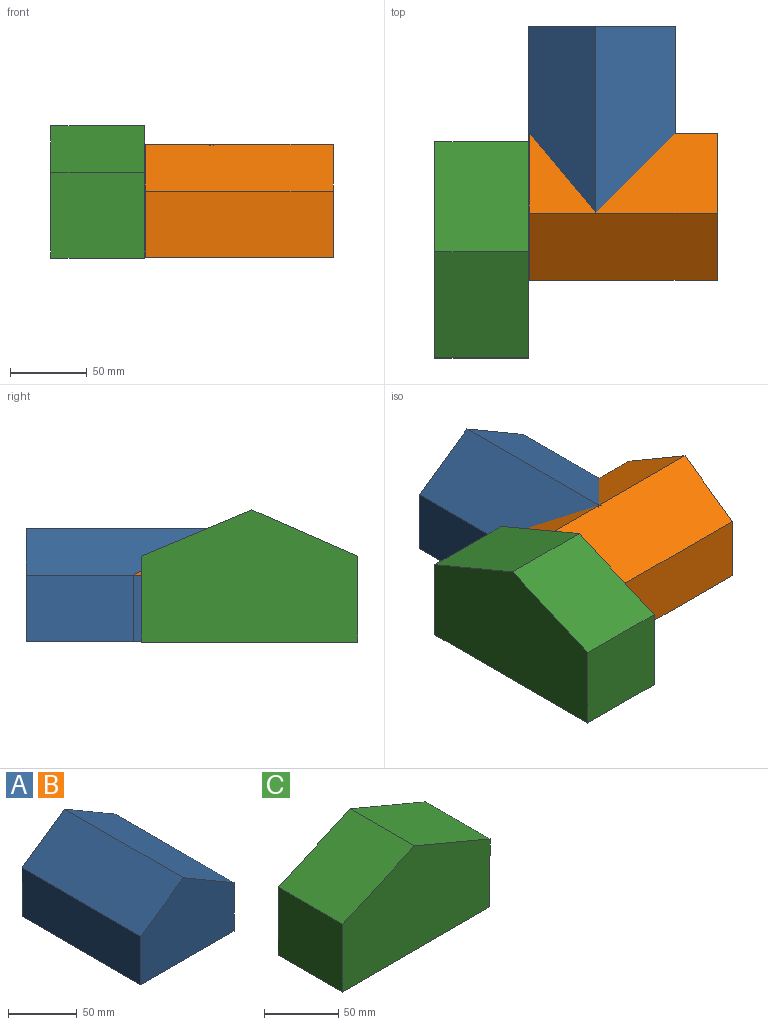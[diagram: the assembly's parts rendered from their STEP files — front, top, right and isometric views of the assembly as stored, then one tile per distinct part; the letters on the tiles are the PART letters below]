
ASSEMBLY  parts=3 mates=3
PART A: 7 faces, bbox 95.5x121.9x73.4 mm
  f0: plane 121.92x43.51mm, normal (-0.57,0,0.82), area 6476.6mm2, adj f1,f4,f5,f6
  f1: plane 121.92x42.97mm, normal (-1,0,0), area 5238.6mm2, adj f0,f2,f5,f6
  f2: plane 121.92x95.52mm, normal (0,0,-1), area 11645.4mm2, adj f1,f3,f5,f6
  f3: plane 121.92x42.97mm, normal (1,0,0), area 5238.6mm2, adj f2,f4,f5,f6
  f4: plane 121.92x52mm, normal (0.51,0,0.86), area 7348.2mm2, adj f0,f3,f5,f6
  f5: plane 95.52x73.44mm, normal (0,-1,0), area 5559.3mm2, adj f0,f1,f2,f3,f4
  f6: plane 95.52x73.44mm, normal (0,1,0), area 5559.3mm2, adj f0,f1,f2,f3,f4
PART B: same geometry as A
PART C: 7 faces, bbox 140.3x61x85.8 mm
  f0: plane 68.82x60.96mm, normal (-0.4,0,0.92), area 4577.2mm2, adj f1,f4,f5,f6
  f1: plane 60.96x55.82mm, normal (-1,0,0), area 3402.9mm2, adj f0,f2,f5,f6
  f2: plane 140.33x60.96mm, normal (0,0,-1), area 8554.5mm2, adj f1,f3,f5,f6
  f3: plane 60.96x55.82mm, normal (1,0,0), area 3402.9mm2, adj f2,f4,f5,f6
  f4: plane 71.51x60.96mm, normal (0.39,0,0.92), area 4727.6mm2, adj f0,f3,f5,f6
  f5: plane 140.33x85.84mm, normal (0,-1,0), area 9939.8mm2, adj f0,f1,f2,f3,f4
  f6: plane 140.33x85.84mm, normal (0,1,0), area 9939.8mm2, adj f0,f1,f2,f3,f4
PLACE A t=(46.76,105.11,-33.08)mm
PLACE B rot(axis=(0,0,1),90deg) t=(-45.16,32.32,-33.01)mm
PLACE C rot(axis=(0,0,1),90deg) t=(-106.63,29.91,-33.53)mm
MATE parallel C.f6 <-> A.f1  axis (-1,0,0) through (-106.63,-40.35,2.42)mm
MATE parallel B.f5 <-> A.f3  axis (1,0,0) through (76.76,-12.55,-3.24)mm
MATE parallel B.f2 <-> A.f2  axis (0,0,-1) through (15.8,-12.18,-33.01)mm
